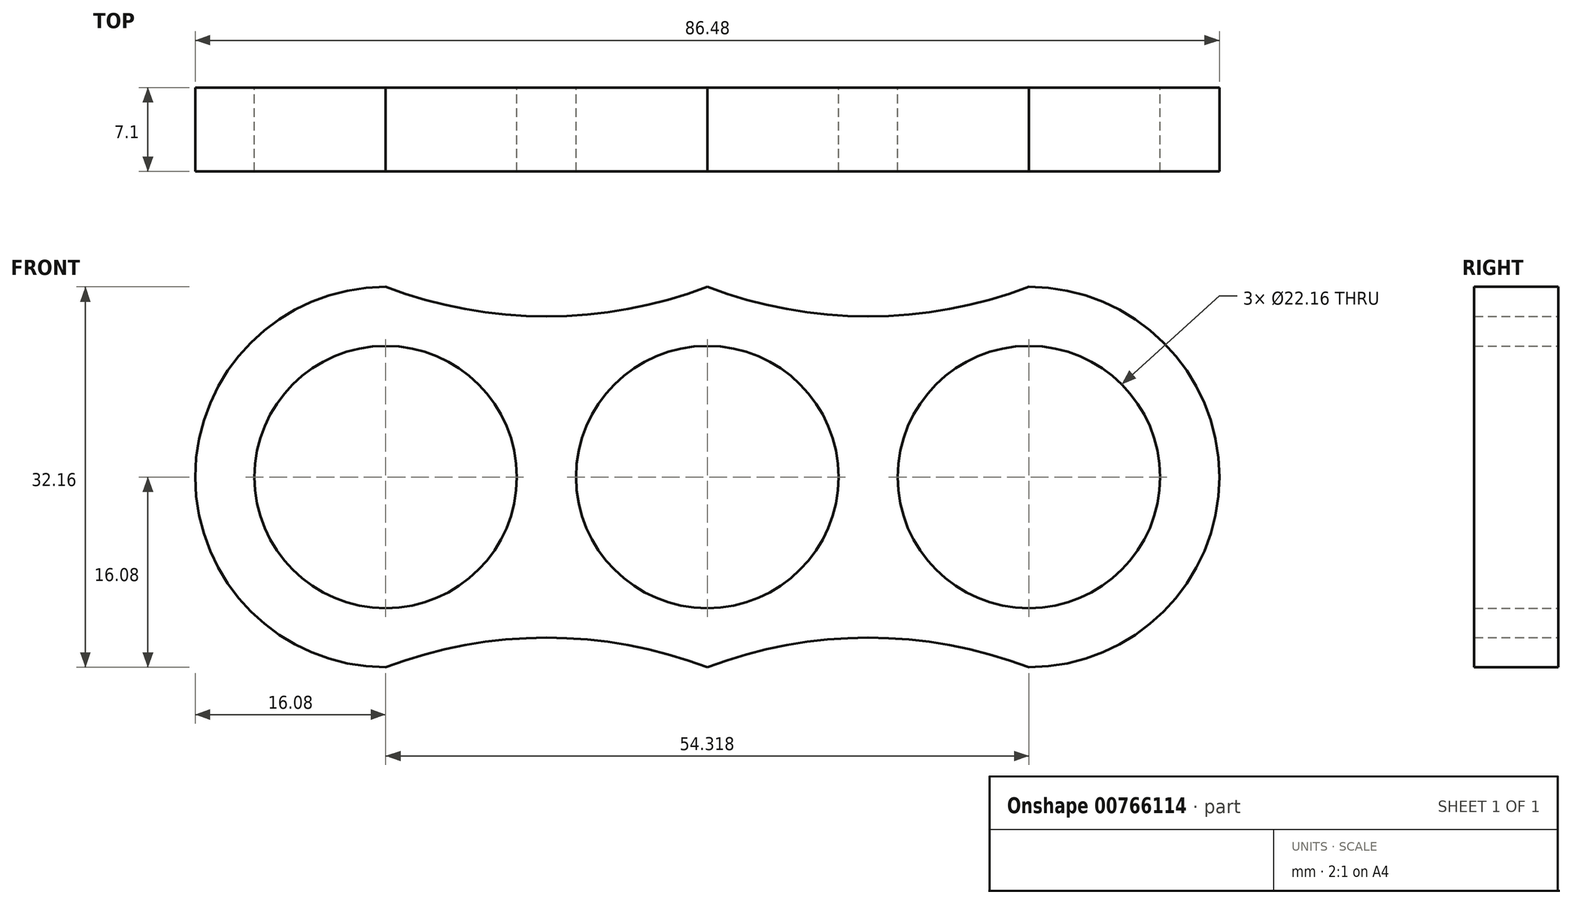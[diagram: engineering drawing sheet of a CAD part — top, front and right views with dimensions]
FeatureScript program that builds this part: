
annotation { "Feature Type Name" : "Feature", "Feature Type Description" : "" }
export const myFeature = defineFeature(function(context is Context, id is Id, definition is map)
    precondition{}
    {
        {
            var Q0;
            Q0=qCreatedBy(makeId("Front.planeOp"),FACE);
            var sketch = newSketch(context, id + "F0", { "sketchPlane" : qUnion([Q0])});
            skCircle(sketch, "E0", {"center": v(0, 0) * mm, "radius": 11.08 * mm});
            skLineSegment(sketch, "E1", {"start": v(11.08, 0) * mm, "end": v(16.08, 0) * mm});
            skPoint(sketch, "E2.endSnap0", {"position": v(13.58, 0) * mm});
            skCircle(sketch, "E3", {"center": v(27.16, 0) * mm, "radius": 11.08 * mm});
            skLineSegment(sketch, "E4", {"start": v(-11.08, 0) * mm, "end": v(-16.08, 0) * mm});
            skCircle(sketch, "E5", {"center": v(-27.16, 0) * mm, "radius": 11.08 * mm});
            skLineSegment(sketch, "E6", {"start": v(43.24, 0) * mm, "end": v(43.24, 0) * mm});
            skLineSegment(sketch, "E7", {"start": v(-43.24, 0) * mm, "end": v(-43.24, 0) * mm});
            skPoint(sketch, "E8.orphan", {"position": v(-43.24, 16.08) * mm});
            skPoint(sketch, "E9.orphan", {"position": v(-43.23, -16.08) * mm});
            skPoint(sketch, "E10.orphan", {"position": v(43.24, 16.08) * mm});
            skPoint(sketch, "E11.orphan", {"position": v(43.24, -16.08) * mm});
            skPoint(sketch, "E12.start.orphan", {"position": v(38.24, 0) * mm});
            skPoint(sketch, "E13.start.orphan", {"position": v(-38.24, 0) * mm});
            skPoint(sketch, "E14.start.orphan", {"position": v(-27.16, -11.08) * mm});
            skPoint(sketch, "E15.start.orphan", {"position": v(0, -11.08) * mm});
            skPoint(sketch, "E16.start.orphan", {"position": v(0, 11.08) * mm});
            skPoint(sketch, "E17.end.orphan", {"position": v(-11.08, -16.08) * mm});
            skPoint(sketch, "E18.end.orphan", {"position": v(0, -16.08) * mm});
            skPoint(sketch, "E19.start.orphan", {"position": v(-27.16, -16.08) * mm});
            skPoint(sketch, "E20.start.orphan", {"position": v(-27.16, 11.08) * mm});
            skPoint(sketch, "E21.end.orphan", {"position": v(0, 16.08) * mm});
            skPoint(sketch, "E22.start.orphan", {"position": v(27.16, 11.08) * mm});
            skArc(sketch, "E23", {"start": v(-27.16, 16.08) * mm, "mid": v(-43.24, 0) * mm, "end": v(-27.16, -16.08) * mm});
            skArc(sketch, "E24", {"start": v(27.16, -16.08) * mm, "mid": v(43.24, 0) * mm, "end": v(27.16, 16.08) * mm});
            skPoint(sketch, "E25.end.orphan", {"position": v(27.16, 18.58) * mm});
            skPoint(sketch, "E26.orphan", {"position": v(-27.16, 18.58) * mm});
            skPoint(sketch, "E27.start.orphan", {"position": v(27.16, -11.08) * mm});
            skArc(sketch, "E28", {"start": v(0, 16.08) * mm, "mid": v(13.58, 13.58) * mm, "end": v(27.16, 16.08) * mm});
            skArc(sketch, "E29", {"start": v(-27.16, 16.08) * mm, "mid": v(-13.58, 13.58) * mm, "end": v(0, 16.08) * mm});
            skPoint(sketch, "E30.start.orphan", {"position": v(-13.58, 16.08) * mm});
            skPoint(sketch, "E31.start.orphan", {"position": v(13.58, 16.08) * mm});
            skArc(sketch, "E32", {"start": v(0, -16.08) * mm, "mid": v(-13.58, -13.58) * mm, "end": v(-27.16, -16.08) * mm});
            skPoint(sketch, "E33.start.orphan", {"position": v(-13.58, -16.08) * mm});
            skArc(sketch, "E34", {"start": v(27.16, -16.08) * mm, "mid": v(13.58, -13.58) * mm, "end": v(0, -16.08) * mm});
            skPoint(sketch, "E35.start.orphan", {"position": v(13.58, -16.08) * mm});
            skSolve(sketch);
        }
        {
            var Q0;
            Q0 = qSketchRegion(id + "F0", true);
            extrude(context, id + "F1", {"entities" : qUnion([Q0]), "depth" : 7.1 * mm, "offsetDistance" : 25 * mm});
        }
    });
